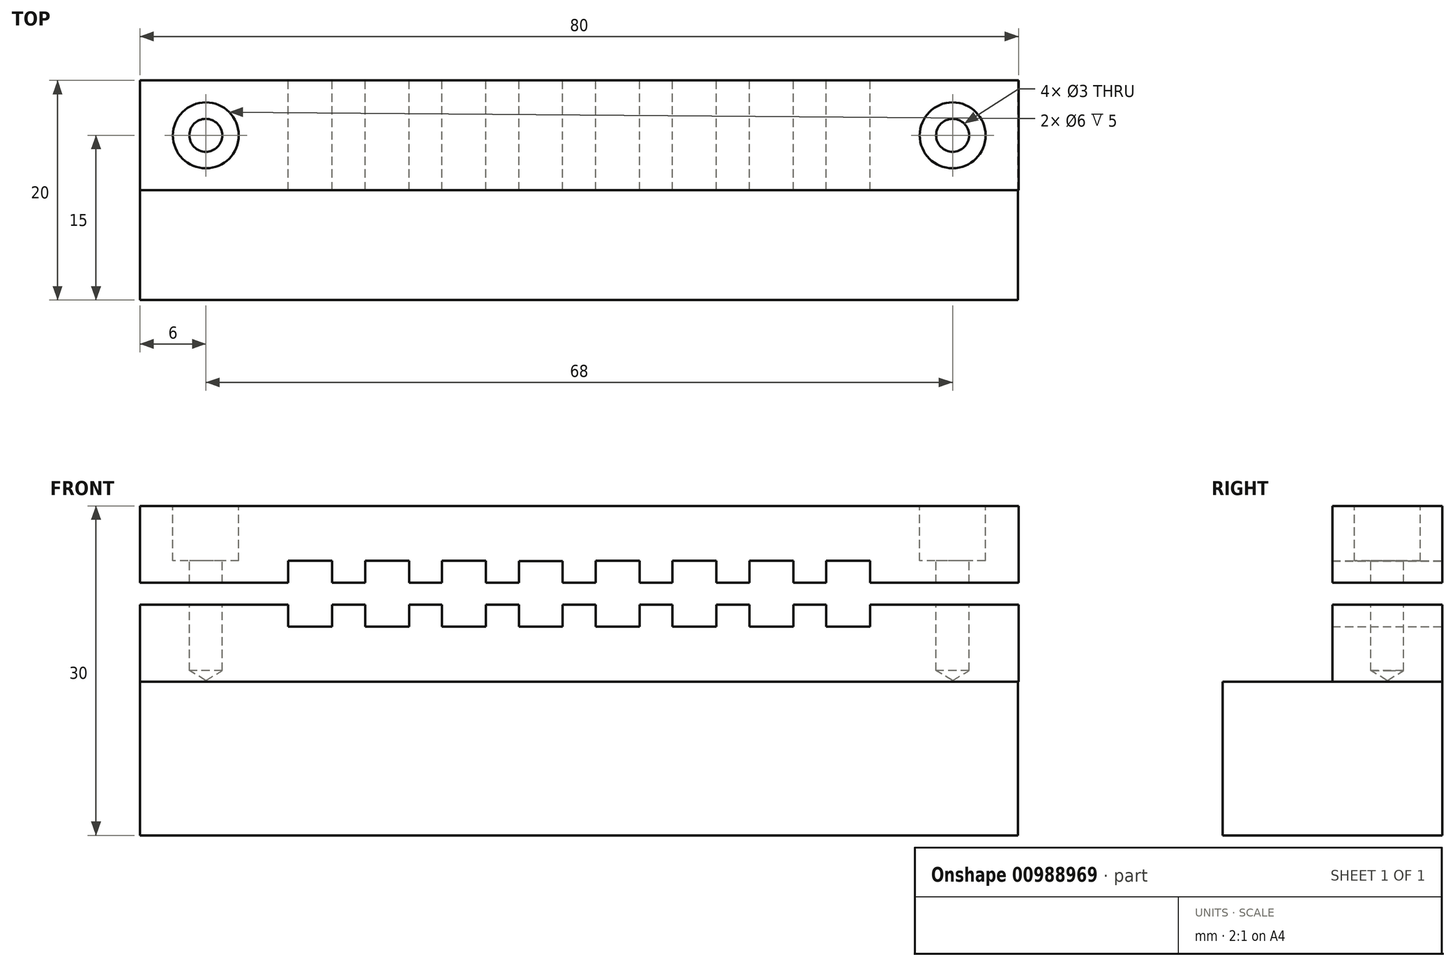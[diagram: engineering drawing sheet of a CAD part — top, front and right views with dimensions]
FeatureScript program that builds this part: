
annotation { "Feature Type Name" : "Feature", "Feature Type Description" : "" }
export const myFeature = defineFeature(function(context is Context, id is Id, definition is map)
    precondition{}
    {
        {
            var Q0;
            Q0=qCreatedBy(makeId("Front.planeOp"),FACE);
            var sketch = newSketch(context, id + "F0", { "sketchPlane" : qUnion([Q0])});
            skLineSegment(sketch, "E0.bottom", {"start": v(0, 0) * mm, "end": v(80, 0) * mm});
            skLineSegment(sketch, "E0.top", {"start": v(0, 7) * mm, "end": v(80, 7) * mm});
            skLineSegment(sketch, "E0.left", {"start": v(0, 0) * mm, "end": v(0, 7) * mm});
            skLineSegment(sketch, "E0.right", {"start": v(80, 0) * mm, "end": v(80, 7) * mm});
            skLineSegment(sketch, "E1.bottom", {"start": v(13.5, 7) * mm, "end": v(17.5, 7) * mm});
            skLineSegment(sketch, "E1.top", {"start": v(13.5, 5) * mm, "end": v(17.5, 5) * mm});
            skLineSegment(sketch, "E1.left", {"start": v(13.5, 7) * mm, "end": v(13.5, 5) * mm});
            skLineSegment(sketch, "E1.right", {"start": v(17.5, 7) * mm, "end": v(17.5, 5) * mm});
            skLineSegment(sketch, "E2.top", {"start": v(20.5, 5) * mm, "end": v(24.5, 5) * mm});
            skLineSegment(sketch, "E2.left", {"start": v(20.5, 7) * mm, "end": v(20.5, 5) * mm});
            skLineSegment(sketch, "E2.right", {"start": v(24.5, 7) * mm, "end": v(24.5, 5) * mm});
            skLineSegment(sketch, "E3.top", {"start": v(27.5, 5) * mm, "end": v(31.5, 5) * mm});
            skLineSegment(sketch, "E3.left", {"start": v(27.5, 7) * mm, "end": v(27.5, 5) * mm});
            skLineSegment(sketch, "E3.right", {"start": v(31.5, 7) * mm, "end": v(31.5, 5) * mm});
            skLineSegment(sketch, "E4.top", {"start": v(34.5, 5.01) * mm, "end": v(38.5, 5.01) * mm});
            skLineSegment(sketch, "E4.left", {"start": v(34.5, 7.01) * mm, "end": v(34.5, 5.01) * mm});
            skLineSegment(sketch, "E4.right", {"start": v(38.5, 7.01) * mm, "end": v(38.5, 5.01) * mm});
            skLineSegment(sketch, "E5.top", {"start": v(41.5, 5) * mm, "end": v(45.5, 5) * mm});
            skLineSegment(sketch, "E5.left", {"start": v(41.5, 7) * mm, "end": v(41.5, 5) * mm});
            skLineSegment(sketch, "E5.right", {"start": v(45.5, 7) * mm, "end": v(45.5, 5) * mm});
            skLineSegment(sketch, "E6.top", {"start": v(48.5, 5) * mm, "end": v(52.5, 5) * mm});
            skLineSegment(sketch, "E6.left", {"start": v(48.5, 7) * mm, "end": v(48.5, 5) * mm});
            skLineSegment(sketch, "E6.right", {"start": v(52.5, 7) * mm, "end": v(52.5, 5) * mm});
            skLineSegment(sketch, "E7.top", {"start": v(62.5, 5) * mm, "end": v(66.5, 5) * mm});
            skLineSegment(sketch, "E7.left", {"start": v(62.5, 7) * mm, "end": v(62.5, 5) * mm});
            skLineSegment(sketch, "E7.right", {"start": v(66.5, 7) * mm, "end": v(66.5, 5) * mm});
            skLineSegment(sketch, "E8.top", {"start": v(55.5, 5) * mm, "end": v(59.5, 5) * mm});
            skLineSegment(sketch, "E8.left", {"start": v(55.5, 7) * mm, "end": v(55.5, 5) * mm});
            skLineSegment(sketch, "E8.right", {"start": v(59.5, 7) * mm, "end": v(59.5, 5) * mm});
            skLineSegment(sketch, "E9", {"start": v(0, 8) * mm, "end": v(79.95, 8) * mm, "construction": true});
            skLineSegment(sketch, "E10.MirrorCS", {"start": v(13.5, 9) * mm, "end": v(13.5, 11) * mm});
            skLineSegment(sketch, "E11.MirrorCS", {"start": v(17.5, 9) * mm, "end": v(17.5, 11) * mm});
            skLineSegment(sketch, "E12.MirrorCS", {"start": v(55.5, 9) * mm, "end": v(55.5, 11) * mm});
            skLineSegment(sketch, "E13.MirrorCS", {"start": v(41.5, 9) * mm, "end": v(41.5, 11) * mm});
            skLineSegment(sketch, "E14.MirrorCS", {"start": v(52.5, 9) * mm, "end": v(52.5, 11) * mm});
            skLineSegment(sketch, "E15.MirrorCS", {"start": v(27.5, 9) * mm, "end": v(27.5, 11) * mm});
            skLineSegment(sketch, "E16.MirrorCS", {"start": v(48.5, 9) * mm, "end": v(48.5, 11) * mm});
            skLineSegment(sketch, "E17.MirrorCS", {"start": v(66.5, 9) * mm, "end": v(66.5, 11) * mm});
            skLineSegment(sketch, "E18.MirrorCS", {"start": v(45.5, 9) * mm, "end": v(45.5, 11) * mm});
            skLineSegment(sketch, "E19.MirrorCS", {"start": v(62.5, 9) * mm, "end": v(62.5, 11) * mm});
            skLineSegment(sketch, "E20.MirrorCS", {"start": v(38.5, 8.99) * mm, "end": v(38.5, 10.99) * mm});
            skLineSegment(sketch, "E21.MirrorCS", {"start": v(24.5, 9) * mm, "end": v(24.5, 11) * mm});
            skLineSegment(sketch, "E22.MirrorCS", {"start": v(34.5, 8.99) * mm, "end": v(34.5, 10.99) * mm});
            skLineSegment(sketch, "E23.MirrorCS", {"start": v(31.5, 9) * mm, "end": v(31.5, 11) * mm});
            skLineSegment(sketch, "E24.MirrorCS", {"start": v(59.5, 9) * mm, "end": v(59.5, 11) * mm});
            skLineSegment(sketch, "E25.MirrorCS", {"start": v(20.5, 9) * mm, "end": v(20.5, 11) * mm});
            skLineSegment(sketch, "E26.MirrorCS", {"start": v(55.5, 11) * mm, "end": v(59.5, 11) * mm});
            skLineSegment(sketch, "E27.MirrorCS", {"start": v(80, 16) * mm, "end": v(80, 9) * mm});
            skLineSegment(sketch, "E28.MirrorCS", {"start": v(41.5, 11) * mm, "end": v(45.5, 11) * mm});
            skLineSegment(sketch, "E29.MirrorCS", {"start": v(0, 16) * mm, "end": v(0, 9) * mm});
            skLineSegment(sketch, "E30.MirrorCS", {"start": v(13.5, 11) * mm, "end": v(17.5, 11) * mm});
            skLineSegment(sketch, "E31.MirrorCS", {"start": v(48.5, 11) * mm, "end": v(52.5, 11) * mm});
            skLineSegment(sketch, "E32.MirrorCS", {"start": v(62.5, 11) * mm, "end": v(66.5, 11) * mm});
            skLineSegment(sketch, "E33.MirrorCS", {"start": v(13.5, 9) * mm, "end": v(17.5, 9) * mm});
            skLineSegment(sketch, "E34.MirrorCS", {"start": v(0, 9) * mm, "end": v(80, 9) * mm});
            skLineSegment(sketch, "E35.MirrorCS", {"start": v(0, 16) * mm, "end": v(80, 16) * mm});
            skLineSegment(sketch, "E36.MirrorCS", {"start": v(27.5, 11) * mm, "end": v(31.5, 11) * mm});
            skLineSegment(sketch, "E37.MirrorCS", {"start": v(20.5, 11) * mm, "end": v(24.5, 11) * mm});
            skLineSegment(sketch, "E38.MirrorCS", {"start": v(34.5, 10.99) * mm, "end": v(38.5, 10.99) * mm});
            skLineSegment(sketch, "E39.bottom", {"start": v(0, 0) * mm, "end": v(79.94, 0) * mm});
            skLineSegment(sketch, "E39.top", {"start": v(0, -14) * mm, "end": v(79.94, -14) * mm});
            skLineSegment(sketch, "E39.left", {"start": v(0, 0) * mm, "end": v(0, -14) * mm});
            skLineSegment(sketch, "E39.right", {"start": v(79.94, 0) * mm, "end": v(79.94, -14) * mm});
            skSolve(sketch);
        }
        {
            var Q0;
            {var subQ18=sQuery(id+"F0.wireOp",EDGE,"E10.MirrorCS");Q0=makeQuery(id+"F0.imprint","IMPRINT",FACE,{"disambiguationData":[TD([[makeQuery(id+"F0.imprint","IMPRINT",EDGE,{"derivedFrom":subQ18}),1.0]])]});}
            var Q1;
            {var subQ4=sQuery(id+"F0.wireOp",EDGE,"E0.left");Q1=makeQuery(id+"F0.imprint","IMPRINT",FACE,{"disambiguationData":[TD([[makeQuery(id+"F0.imprint","IMPRINT",EDGE,{"derivedFrom":subQ4}),-1.0]])]});}
            extrude(context, id + "F1", {"entities" : qUnion([Q0, Q1]), "depth" : 10 * mm, "offsetDistance" : 25 * mm});
        }
        {
            var Q0;
            Q0=makeQuery(id+"F1.opExtrude","SWEPT_FACE",FACE,{"disambiguationData":[OSD([sQuery(id+"F0.wireOp",EDGE,"E35.MirrorCS")])]});
            var sketch = newSketch(context, id + "F2", { "sketchPlane" : qUnion([Q0])});
            skPoint(sketch, "E40", {"position": v(6, -5) * mm});
            skPoint(sketch, "E40.positionSnap0", {"position": v(0, -5) * mm});
            skPoint(sketch, "E41", {"position": v(74, -5) * mm});
            skSolve(sketch);
        }
        {
            var Q0;
            Q0=sQuery(id+"F2.wireOp",VERTEX,"E40");
            var Q1;
            Q1=sQuery(id+"F2.wireOp",VERTEX,"E41");
            var Q2;
            Q2=makeQuery(id+"F1.opExtrude","SWEPT_BODY",BODY,{"disambiguationData":[OSD([sQuery(id+"F0.wireOp",EDGE,"E0.bottom"),sQuery(id+"F0.wireOp",EDGE,"E0.top"),sQuery(id+"F0.wireOp",EDGE,"E0.left"),sQuery(id+"F0.wireOp",EDGE,"E0.right"),sQuery(id+"F0.wireOp",EDGE,"E1.top"),sQuery(id+"F0.wireOp",EDGE,"E1.left"),sQuery(id+"F0.wireOp",EDGE,"E1.right"),sQuery(id+"F0.wireOp",EDGE,"E2.top"),sQuery(id+"F0.wireOp",EDGE,"E2.left"),sQuery(id+"F0.wireOp",EDGE,"E2.right"),sQuery(id+"F0.wireOp",EDGE,"E3.top"),sQuery(id+"F0.wireOp",EDGE,"E3.left"),sQuery(id+"F0.wireOp",EDGE,"E3.right"),sQuery(id+"F0.wireOp",EDGE,"E4.top"),sQuery(id+"F0.wireOp",EDGE,"E4.left"),sQuery(id+"F0.wireOp",EDGE,"E4.right"),sQuery(id+"F0.wireOp",EDGE,"E5.top"),sQuery(id+"F0.wireOp",EDGE,"E5.left"),sQuery(id+"F0.wireOp",EDGE,"E5.right"),sQuery(id+"F0.wireOp",EDGE,"E6.top"),sQuery(id+"F0.wireOp",EDGE,"E6.left"),sQuery(id+"F0.wireOp",EDGE,"E6.right"),sQuery(id+"F0.wireOp",EDGE,"E7.top"),sQuery(id+"F0.wireOp",EDGE,"E7.left"),sQuery(id+"F0.wireOp",EDGE,"E7.right"),sQuery(id+"F0.wireOp",EDGE,"E8.top"),sQuery(id+"F0.wireOp",EDGE,"E8.left"),sQuery(id+"F0.wireOp",EDGE,"E8.right")])]});
            var Q3;
            Q3=makeQuery(id+"F1.opExtrude","SWEPT_BODY",BODY,{"disambiguationData":[OSD([sQuery(id+"F0.wireOp",EDGE,"E10.MirrorCS"),sQuery(id+"F0.wireOp",EDGE,"E11.MirrorCS"),sQuery(id+"F0.wireOp",EDGE,"E12.MirrorCS"),sQuery(id+"F0.wireOp",EDGE,"E13.MirrorCS"),sQuery(id+"F0.wireOp",EDGE,"E14.MirrorCS"),sQuery(id+"F0.wireOp",EDGE,"E15.MirrorCS"),sQuery(id+"F0.wireOp",EDGE,"E16.MirrorCS"),sQuery(id+"F0.wireOp",EDGE,"E17.MirrorCS"),sQuery(id+"F0.wireOp",EDGE,"E18.MirrorCS"),sQuery(id+"F0.wireOp",EDGE,"E19.MirrorCS"),sQuery(id+"F0.wireOp",EDGE,"E20.MirrorCS"),sQuery(id+"F0.wireOp",EDGE,"E21.MirrorCS"),sQuery(id+"F0.wireOp",EDGE,"E22.MirrorCS"),sQuery(id+"F0.wireOp",EDGE,"E23.MirrorCS"),sQuery(id+"F0.wireOp",EDGE,"E24.MirrorCS"),sQuery(id+"F0.wireOp",EDGE,"E25.MirrorCS"),sQuery(id+"F0.wireOp",EDGE,"E26.MirrorCS"),sQuery(id+"F0.wireOp",EDGE,"E27.MirrorCS"),sQuery(id+"F0.wireOp",EDGE,"E28.MirrorCS"),sQuery(id+"F0.wireOp",EDGE,"E29.MirrorCS"),sQuery(id+"F0.wireOp",EDGE,"E30.MirrorCS"),sQuery(id+"F0.wireOp",EDGE,"E31.MirrorCS"),sQuery(id+"F0.wireOp",EDGE,"E32.MirrorCS"),sQuery(id+"F0.wireOp",EDGE,"E34.MirrorCS"),sQuery(id+"F0.wireOp",EDGE,"E35.MirrorCS"),sQuery(id+"F0.wireOp",EDGE,"E36.MirrorCS"),sQuery(id+"F0.wireOp",EDGE,"E37.MirrorCS"),sQuery(id+"F0.wireOp",EDGE,"E38.MirrorCS")])]});
            hole(context, id + "F3", {"style" : HoleStyle.C_BORE, "endStyle" : HoleEndStyle.BLIND, "holeDiameter" : 3 * mm, "cBoreDiameter" : 6 * mm, "cBoreDepth" : 5 * mm, "majorDiameter" : 5 * mm, "holeDepth" : 15 * mm, "isTappedThrough" : true, "tappedDepth" : 12 * mm, "tapClearance" : 3, "locations" : qUnion([Q0, Q1]), "scope" : qUnion([Q2, Q3])});
        }
        {
            var Q0;
            Q0=makeQuery(id+"F0.imprint","IMPRINT",FACE,{"disambiguationData":[TD([[makeQuery(id+"F0.imprint","IMPRINT",EDGE,{"derivedFrom":sQuery(id+"F0.wireOp",EDGE,"E39.top")}),1.0]])]});
            extrude(context, id + "F4", {"entities" : qUnion([Q0]), "operationType" : NewBodyOperationType.ADD, "depth" : 20 * mm, "offsetDistance" : 25 * mm});
        }
    });
